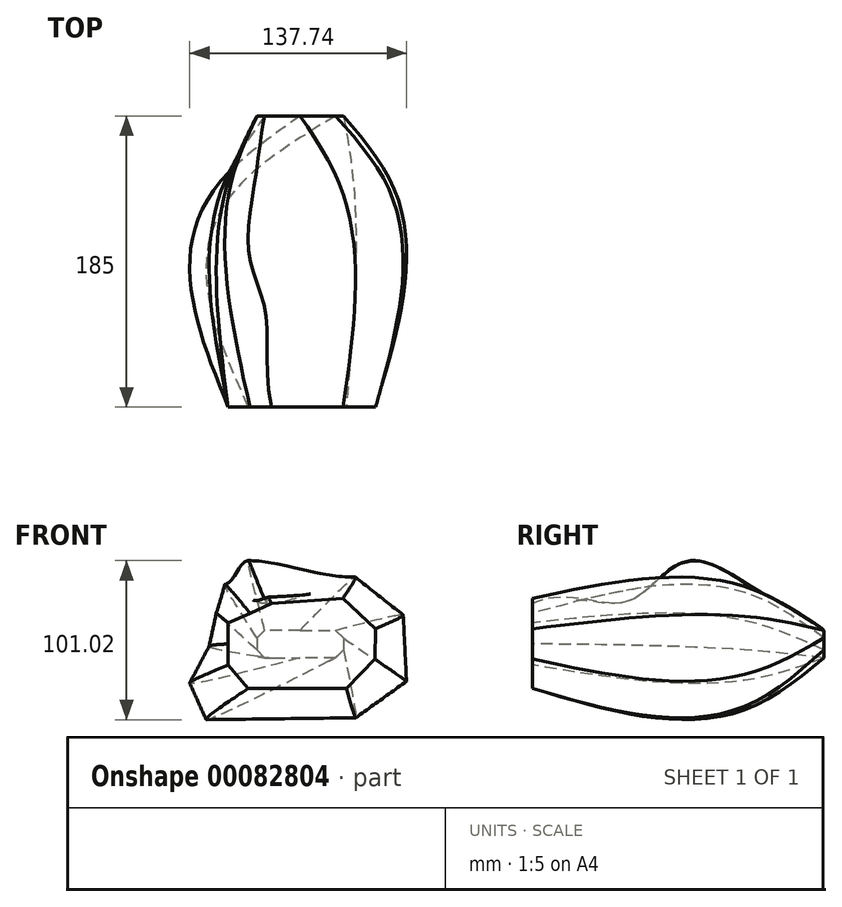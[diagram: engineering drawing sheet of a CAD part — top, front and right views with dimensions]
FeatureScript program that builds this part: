
annotation { "Feature Type Name" : "Feature", "Feature Type Description" : "" }
export const myFeature = defineFeature(function(context is Context, id is Id, definition is map)
    precondition{}
    {
        {
            var Q0;
            Q0=qCreatedBy(makeId("Front.planeOp"),FACE);
            cPlane(context, id + "F0", {"entities" : qUnion([Q0]), "cplaneType" : CPlaneType.OFFSET, "offset" : 185 * mm, "width" : 150 * mm, "height" : 150 * mm});
        }
        {
            var Q0;
            Q0=qCreatedBy(makeId("Front.planeOp"),FACE);
            cPlane(context, id + "F1", {"entities" : qUnion([Q0]), "cplaneType" : CPlaneType.OFFSET, "offset" : 20 * mm, "width" : 150 * mm, "height" : 150 * mm});
        }
        {
            var Q0;
            Q0=qCreatedBy(makeId("Front.planeOp"),FACE);
            cPlane(context, id + "F2", {"entities" : qUnion([Q0]), "cplaneType" : CPlaneType.OFFSET, "offset" : 40 * mm, "width" : 150 * mm, "height" : 150 * mm});
        }
        {
            var Q0;
            Q0=qCreatedBy(makeId("Front.planeOp"),FACE);
            cPlane(context, id + "F3", {"entities" : qUnion([Q0]), "cplaneType" : CPlaneType.OFFSET, "offset" : 160 * mm, "width" : 150 * mm, "height" : 150 * mm});
        }
        {
            var Q0;
            Q0=qCreatedBy(makeId("Front.planeOp"),FACE);
            var sketch = newSketch(context, id + "F4", { "sketchPlane" : qUnion([Q0])});
            skLineSegment(sketch, "E0", {"start": v(0, 8.72) * mm, "end": v(22.5, 8.72) * mm});
            skLineSegment(sketch, "E1", {"start": v(22.5, 8.72) * mm, "end": v(27.5, 3.72) * mm});
            skLineSegment(sketch, "E2", {"start": v(27.5, 3.72) * mm, "end": v(27.5, -3.78) * mm});
            skLineSegment(sketch, "E3", {"start": v(27.5, -3.78) * mm, "end": v(22.5, -8.78) * mm});
            skLineSegment(sketch, "E4", {"start": v(22.5, -8.78) * mm, "end": v(0, -8.78) * mm});
            skLineSegment(sketch, "E5.MirrorCS", {"start": v(0, 8.72) * mm, "end": v(-22.5, 8.72) * mm});
            skLineSegment(sketch, "E6.MirrorCS", {"start": v(-22.5, 8.72) * mm, "end": v(-27.5, 3.72) * mm});
            skLineSegment(sketch, "E7.MirrorCS", {"start": v(-27.5, 3.72) * mm, "end": v(-27.5, -3.78) * mm});
            skLineSegment(sketch, "E8.MirrorCS", {"start": v(-27.5, -3.78) * mm, "end": v(-22.5, -8.78) * mm});
            skLineSegment(sketch, "E9.MirrorCS", {"start": v(-22.5, -8.78) * mm, "end": v(0, -8.78) * mm});
            skSolve(sketch);
        }
        {
            var Q0;
            Q0=qCreatedBy(id+"F1.planeOp",FACE);
            var sketch = newSketch(context, id + "F5", { "sketchPlane" : qUnion([Q0])});
            skFitSpline(sketch, "E10", {"points": [v(-18.58, 24.76) * mm, v(-53.54, 0) * mm, v(-18.86, -54.76) * mm, v(37.03, -55) * mm, v(55.26, 12.46) * mm, v(-18.58, 24.76) * mm]});
            skSolve(sketch);
        }
        {
            var Q0;
            Q0=qCreatedBy(id+"F3.planeOp",FACE);
            var sketch = newSketch(context, id + "F6", { "sketchPlane" : qUnion([Q0])});
            skFitSpline(sketch, "E11", {"points": [v(-68.1, 36.7) * mm, v(13.04, 55.05) * mm, v(105.76, -22.21) * mm, v(23.18, -100.45) * mm, v(-63.26, -62.3) * mm, v(-78.7, -8.5) * mm, v(-68.1, 36.7) * mm]});
            skSolve(sketch);
        }
        {
            var Q0;
            Q0=qCreatedBy(id+"F2.planeOp",FACE);
            var sketch = newSketch(context, id + "F7", { "sketchPlane" : qUnion([Q0])});
            skFitSpline(sketch, "E12", {"points": [v(-24.05, 39.26) * mm, v(-59.01, 14.5) * mm, v(-24.33, -40.26) * mm, v(31.56, -40.5) * mm, v(49.8, 26.95) * mm, v(-24.05, 39.26) * mm]});
            skSolve(sketch);
        }
        {
            var Q0;
            Q0=qCreatedBy(id+"F0.planeOp",FACE);
            var sketch = newSketch(context, id + "F8", { "sketchPlane" : qUnion([Q0])});
            skLineSegment(sketch, "E13", {"start": v(-45.72, 13.38) * mm, "end": v(-18.21, 25.65) * mm});
            skLineSegment(sketch, "E14", {"start": v(-18.21, 25.65) * mm, "end": v(27.13, 29) * mm});
            skLineSegment(sketch, "E15", {"start": v(27.13, 29) * mm, "end": v(47.95, 9.66) * mm});
            skLineSegment(sketch, "E16", {"start": v(47.95, 9.66) * mm, "end": v(47.57, -9.66) * mm});
            skLineSegment(sketch, "E17", {"start": v(47.57, -9.66) * mm, "end": v(29.36, -28.25) * mm});
            skLineSegment(sketch, "E18", {"start": v(29.36, -28.25) * mm, "end": v(-33.08, -28.25) * mm});
            skLineSegment(sketch, "E19", {"start": v(-33.08, -28.25) * mm, "end": v(-45.72, -13.38) * mm});
            skLineSegment(sketch, "E20", {"start": v(-45.72, -13.38) * mm, "end": v(-45.72, 13.38) * mm});
            skSolve(sketch);
        }
        {
            var Q0;
            Q0=qCreatedBy(id+"F2.planeOp",FACE);
            var sketch = newSketch(context, id + "F9", { "sketchPlane" : qUnion([Q0])});
            skLineSegment(sketch, "E21", {"start": v(-43.27, 28.8) * mm, "end": v(-28.52, 32.7) * mm});
            skLineSegment(sketch, "E22", {"start": v(-28.52, 32.7) * mm, "end": v(23.55, 32.7) * mm});
            skLineSegment(sketch, "E23", {"start": v(23.55, 32.7) * mm, "end": v(53.07, 16.54) * mm});
            skLineSegment(sketch, "E24", {"start": v(53.07, 16.54) * mm, "end": v(56.69, -16.31) * mm});
            skLineSegment(sketch, "E25", {"start": v(56.69, -16.31) * mm, "end": v(33.58, -34.7) * mm});
            skLineSegment(sketch, "E26", {"start": v(33.58, -34.7) * mm, "end": v(-34.64, -37.48) * mm});
            skLineSegment(sketch, "E27", {"start": v(-34.64, -37.48) * mm, "end": v(-49.12, -21.33) * mm});
            skLineSegment(sketch, "E28", {"start": v(-49.12, -21.33) * mm, "end": v(-43.27, 28.8) * mm});
            skSolve(sketch);
        }
        {
            var Q0;
            Q0=sQuery(id+"F4.wireOp",VERTEX,"E6.MirrorCS.start");
            var Q1;
            Q1=sQuery(id+"F9.wireOp",VERTEX,"E22.start");
            var Q2;
            Q2=sQuery(id+"F8.wireOp",VERTEX,"E14.start");
            cPlane(context, id + "F10", {"entities" : qUnion([Q0, Q1, Q2]), "cplaneType" : CPlaneType.THREE_POINT, "offset" : 150 * mm, "width" : 150 * mm, "height" : 150 * mm});
        }
        {
            var Q0;
            Q0=qCreatedBy(id+"F10.planeOp",FACE);
            var sketch = newSketch(context, id + "F11", { "sketchPlane" : qUnion([Q0])});
            skLineSegment(sketch, "E29.0.0", {"start": v(1.24, 0.98) * mm, "end": v(0.15, 8.25) * mm, "construction": true});
            skLineSegment(sketch, "E29.0.1", {"start": v(0.15, 8.25) * mm, "end": v(-0.95, 15.53) * mm, "construction": true});
            skLineSegment(sketch, "E29.0.2", {"start": v(-0.95, 15.53) * mm, "end": v(-1.28, 12.42) * mm, "construction": true});
            skLineSegment(sketch, "E29.0.3", {"start": v(-1.28, 12.42) * mm, "end": v(-1.4, 5.32) * mm, "construction": true});
            skLineSegment(sketch, "E29.0.4", {"start": v(-1.4, 5.32) * mm, "end": v(-1.24, -1.03) * mm, "construction": true});
            skLineSegment(sketch, "E29.0.5", {"start": v(-1.24, -1.03) * mm, "end": v(-0.15, -8.3) * mm, "construction": true});
            skLineSegment(sketch, "E29.0.6", {"start": v(-0.15, -8.3) * mm, "end": v(0.95, -15.58) * mm, "construction": true});
            skLineSegment(sketch, "E29.0.7", {"start": v(0.95, -15.58) * mm, "end": v(1.28, -12.47) * mm, "construction": true});
            skLineSegment(sketch, "E29.0.8", {"start": v(1.28, -12.47) * mm, "end": v(1.4, -5.37) * mm, "construction": true});
            skLineSegment(sketch, "E29.0.9", {"start": v(1.4, -5.37) * mm, "end": v(1.24, 0.98) * mm, "construction": true});
            skLineSegment(sketch, "E30.0.0", {"start": v(39.1, 40.16) * mm, "end": v(38.32, 41.24) * mm, "construction": true});
            skLineSegment(sketch, "E30.0.1", {"start": v(38.32, 41.24) * mm, "end": v(37.2, -4.3) * mm, "construction": true});
            skLineSegment(sketch, "E30.0.2", {"start": v(37.2, -4.3) * mm, "end": v(37.64, -24.25) * mm, "construction": true});
            skLineSegment(sketch, "E30.0.3", {"start": v(37.64, -24.25) * mm, "end": v(41, -43.69) * mm, "construction": true});
            skLineSegment(sketch, "E30.0.4", {"start": v(41, -43.69) * mm, "end": v(42.44, -33.78) * mm, "construction": true});
            skLineSegment(sketch, "E30.0.5", {"start": v(42.44, -33.78) * mm, "end": v(42.8, -1.52) * mm, "construction": true});
            skLineSegment(sketch, "E30.0.6", {"start": v(42.8, -1.52) * mm, "end": v(41.64, 23.31) * mm, "construction": true});
            skLineSegment(sketch, "E30.0.7", {"start": v(41.64, 23.31) * mm, "end": v(39.1, 40.16) * mm, "construction": true});
            skLineSegment(sketch, "E31.0.0", {"start": v(184.3, 30.16) * mm, "end": v(182.75, 27.45) * mm, "construction": true});
            skLineSegment(sketch, "E31.0.1", {"start": v(182.75, 27.45) * mm, "end": v(182.3, 2.13) * mm, "construction": true});
            skLineSegment(sketch, "E31.0.2", {"start": v(182.3, 2.13) * mm, "end": v(182.67, -16.03) * mm, "construction": true});
            skLineSegment(sketch, "E31.0.3", {"start": v(182.67, -16.03) * mm, "end": v(185.71, -36.23) * mm, "construction": true});
            skLineSegment(sketch, "E31.0.4", {"start": v(185.71, -36.23) * mm, "end": v(186.91, -24.53) * mm, "construction": true});
            skLineSegment(sketch, "E31.0.5", {"start": v(186.91, -24.53) * mm, "end": v(187.25, -6.37) * mm, "construction": true});
            skLineSegment(sketch, "E31.0.6", {"start": v(187.25, -6.37) * mm, "end": v(186.56, 18.65) * mm, "construction": true});
            skLineSegment(sketch, "E31.0.7", {"start": v(186.56, 18.65) * mm, "end": v(184.3, 30.16) * mm, "construction": true});
            skFitSpline(sketch, "E32", {"points": [v(-0.95, 15.53) * mm, v(39.1, 40.16) * mm, v(87.05, 60.05) * mm, v(125, 32.36) * mm, v(184.3, 30.16) * mm], "startDerivative": vector(89.29, 83.1) * mm, "endDerivative": vector(258.8, -128.32) * mm});
            skSolve(sketch);
        }
        {
            var Q0;
            Q0=makeQuery(id+"F4.imprint","IMPRINT",FACE,{"disambiguationData":[TD([[makeQuery(id+"F4.imprint","IMPRINT",EDGE,{"derivedFrom":sQuery(id+"F4.wireOp",EDGE,"E0")}),-1.0]])]});
            var Q1;
            Q1=makeQuery(id+"F9.imprint","IMPRINT",FACE,{"disambiguationData":[TD([[makeQuery(id+"F9.imprint","IMPRINT",EDGE,{"derivedFrom":sQuery(id+"F9.wireOp",EDGE,"E21")}),-1.0]])]});
            var Q2;
            Q2=makeQuery(id+"F8.imprint","IMPRINT",FACE,{"disambiguationData":[TD([[makeQuery(id+"F8.imprint","IMPRINT",EDGE,{"derivedFrom":sQuery(id+"F8.wireOp",EDGE,"E13")}),-1.0]])]});
            var Q3;
            Q3=sQuery(id+"F11.wireOp",EDGE,"E32");
            loft(context, id + "F12", {"addGuides" : true, "sheetProfilesArray" : [{ "sheetProfileEntities" : qUnion([Q0]) }, { "sheetProfileEntities" : qUnion([Q1]) }, { "sheetProfileEntities" : qUnion([Q2]) }], "guidesArray" : [{ "guideEntities" : qUnion([Q3]), "guideDerivativeType" : LoftGuideDerivativeType.DEFAULT, "guideDerivativeMagnitude" : 1 }]});
        }
    });
